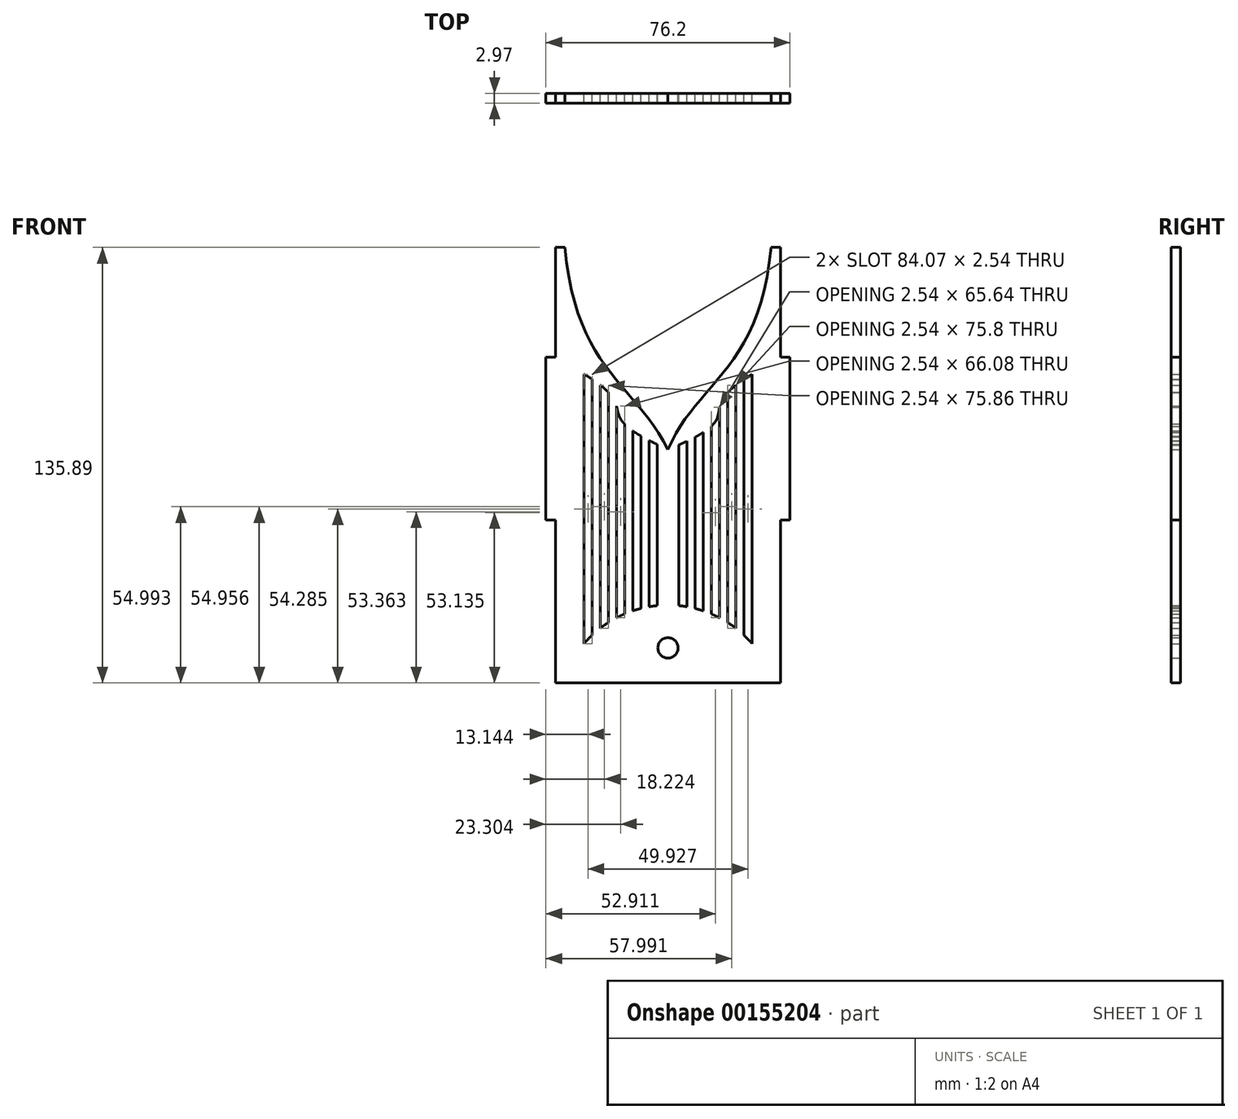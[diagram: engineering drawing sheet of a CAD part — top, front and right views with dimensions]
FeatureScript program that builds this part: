
annotation { "Feature Type Name" : "Feature", "Feature Type Description" : "" }
export const myFeature = defineFeature(function(context is Context, id is Id, definition is map)
    precondition{}
    {
        {
            var Q0;
            Q0=qCreatedBy(makeId("Front.planeOp"),FACE);
            var sketch = newSketch(context, id + "F0", { "sketchPlane" : qUnion([Q0])});
            skLineSegment(sketch, "E0", {"start": v(-13.59, -70.43) * mm, "end": v(56.67, -70.43) * mm});
            skLineSegment(sketch, "E1", {"start": v(-13.59, -70.43) * mm, "end": v(-13.59, 65.46) * mm});
            skLineSegment(sketch, "E2", {"start": v(56.67, -70.43) * mm, "end": v(56.67, 65.46) * mm});
            skLineSegment(sketch, "E3", {"start": v(-13.59, 65.46) * mm, "end": v(56.67, 65.46) * mm});
            skPoint(sketch, "E4.endSnap0", {"position": v(21.45, 21.63) * mm});
            skFitSpline(sketch, "E5", {"points": [v(-7.24, 27.36) * mm, v(-7.24, -61.54) * mm], "startDerivative": vector(0, -83.1) * mm, "endDerivative": vector(0, -83.1) * mm});
            skLineSegment(sketch, "E6", {"start": v(50.32, 27.36) * mm, "end": v(50.32, -61.54) * mm});
            skArc(sketch, "E7", {"start": v(50.32, -61.54) * mm, "mid": v(21.54, -46.15) * mm, "end": v(-7.24, -61.54) * mm});
            skFitSpline(sketch, "E8", {"points": [v(50.32, 27.36) * mm, v(21.54, 2.4) * mm], "startDerivative": vector(-74.85, -42.16) * mm, "endDerivative": vector(-86.33, -35.12) * mm});
            skFitSpline(sketch, "E9", {"points": [v(-7.24, 27.36) * mm, v(21.54, 2.4) * mm], "startDerivative": vector(73.06, -40.73) * mm, "endDerivative": vector(83.73, -37.5) * mm});
            skLineSegment(sketch, "E10", {"start": v(47.78, 25.88) * mm, "end": v(47.78, -58.2) * mm});
            skLineSegment(sketch, "E11", {"start": v(45.24, 24.26) * mm, "end": v(45.24, -55.54) * mm});
            skLineSegment(sketch, "E12", {"start": v(42.7, 22.42) * mm, "end": v(42.7, -53.37) * mm});
            skLineSegment(sketch, "E13", {"start": v(40.16, 20.13) * mm, "end": v(40.16, -51.59) * mm});
            skLineSegment(sketch, "E14", {"start": v(37.62, 15.52) * mm, "end": v(37.62, -50.11) * mm});
            skLineSegment(sketch, "E15", {"start": v(-4.69, 25.9) * mm, "end": v(-4.69, -58.18) * mm});
            skLineSegment(sketch, "E16", {"start": v(-2.15, 24.3) * mm, "end": v(-2.15, -55.53) * mm});
            skLineSegment(sketch, "E17", {"start": v(0.4, 22.5) * mm, "end": v(0.4, -53.37) * mm});
            skLineSegment(sketch, "E18", {"start": v(2.93, 20.25) * mm, "end": v(2.93, -51.58) * mm});
            skLineSegment(sketch, "E19", {"start": v(35.08, 9.62) * mm, "end": v(35.08, -48.9) * mm});
            skLineSegment(sketch, "E20", {"start": v(32.54, 7.7) * mm, "end": v(32.54, -47.95) * mm});
            skLineSegment(sketch, "E21", {"start": v(30, 6.24) * mm, "end": v(30, -47.2) * mm});
            skLineSegment(sketch, "E22", {"start": v(27.46, 4.97) * mm, "end": v(27.46, -46.66) * mm});
            skLineSegment(sketch, "E23", {"start": v(24.92, 3.82) * mm, "end": v(24.92, -46.32) * mm});
            skLineSegment(sketch, "E24", {"start": v(5.47, 15.97) * mm, "end": v(5.47, -50.1) * mm});
            skLineSegment(sketch, "E25", {"start": v(8.01, 10.3) * mm, "end": v(8.01, -48.9) * mm});
            skLineSegment(sketch, "E26", {"start": v(10.55, 8.22) * mm, "end": v(10.55, -47.94) * mm});
            skLineSegment(sketch, "E27", {"start": v(13.1, 6.61) * mm, "end": v(13.1, -47.2) * mm});
            skLineSegment(sketch, "E28", {"start": v(15.63, 5.22) * mm, "end": v(15.63, -46.66) * mm});
            skPoint(sketch, "E29.endSnap0", {"position": v(21.54, -46.15) * mm});
            skLineSegment(sketch, "E30", {"start": v(18.17, 3.96) * mm, "end": v(18.17, -46.32) * mm});
            skLineSegment(sketch, "E31", {"start": v(53.7, 65.46) * mm, "end": v(53.7, -70.43) * mm});
            skLineSegment(sketch, "E32.bottom", {"start": v(53.7, 31.17) * mm, "end": v(56.67, 31.17) * mm});
            skLineSegment(sketch, "E32.top", {"start": v(53.7, -19.63) * mm, "end": v(56.67, -19.63) * mm});
            skLineSegment(sketch, "E32.left", {"start": v(53.7, 31.17) * mm, "end": v(53.7, -19.63) * mm});
            skLineSegment(sketch, "E32.right", {"start": v(56.67, 31.17) * mm, "end": v(56.67, -19.63) * mm});
            skLineSegment(sketch, "E33", {"start": v(-10.61, 65.46) * mm, "end": v(-10.61, -70.43) * mm});
            skLineSegment(sketch, "E34.bottom", {"start": v(-13.59, 31.17) * mm, "end": v(-10.61, 31.17) * mm});
            skLineSegment(sketch, "E34.top", {"start": v(-13.59, -19.63) * mm, "end": v(-10.61, -19.63) * mm});
            skLineSegment(sketch, "E34.left", {"start": v(-13.59, 31.17) * mm, "end": v(-13.59, -19.63) * mm});
            skLineSegment(sketch, "E34.right", {"start": v(-10.61, 31.17) * mm, "end": v(-10.61, -19.63) * mm});
            skCircle(sketch, "E35", {"center": v(21.55, -59.5) * mm, "radius": 3.18 * mm});
            skLineSegment(sketch, "E36.bottom", {"start": v(-13.59, -19.63) * mm, "end": v(-16.56, -19.63) * mm});
            skLineSegment(sketch, "E36.top", {"start": v(-13.59, 31.17) * mm, "end": v(-16.56, 31.17) * mm});
            skLineSegment(sketch, "E36.left", {"start": v(-13.59, -19.63) * mm, "end": v(-13.59, 31.17) * mm});
            skLineSegment(sketch, "E36.right", {"start": v(-16.56, -19.63) * mm, "end": v(-16.56, 31.17) * mm});
            skLineSegment(sketch, "E37.bottom", {"start": v(56.67, 31.17) * mm, "end": v(59.64, 31.17) * mm});
            skLineSegment(sketch, "E37.top", {"start": v(56.67, -19.63) * mm, "end": v(59.64, -19.63) * mm});
            skLineSegment(sketch, "E37.right", {"start": v(59.64, 31.17) * mm, "end": v(59.64, -19.63) * mm});
            skFitSpline(sketch, "E38", {"points": [v(-10.61, 65.46) * mm, v(21.54, 2.4) * mm], "startDerivative": vector(10.13, -114.3) * mm, "endDerivative": vector(32.16, -63.07) * mm});
            skFitSpline(sketch, "E39", {"points": [v(53.7, 65.46) * mm, v(21.54, 2.4) * mm], "startDerivative": vector(-10.13, -114.3) * mm, "endDerivative": vector(-25.29, -61.13) * mm});
            skSolve(sketch);
        }
        {
            var Q0;
            Q0=makeQuery(id+"F0.imprint","IMPRINT",FACE,{"disambiguationData":[TD([[makeQuery(id+"F0.imprint","IMPRINT",EDGE,{"derivedFrom":sQuery(id+"F0.wireOp",EDGE,"E32.bottom")}),-1.0]])]});
            var Q1;
            Q1=makeQuery(id+"F0.imprint","IMPRINT",FACE,{"disambiguationData":[TD([[makeQuery(id+"F0.imprint","IMPRINT",EDGE,{"derivedFrom":sQuery(id+"F0.wireOp",EDGE,"E34.bottom")}),-1.0]])]});
            var Q2;
            Q2=makeQuery(id+"F0.imprint","IMPRINT",FACE,{"disambiguationData":[TD([[makeQuery(id+"F0.imprint","IMPRINT",EDGE,{"derivedFrom":sQuery(id+"F0.wireOp",EDGE,"6379b0e4-c35b-4f8c-ac63-970296725065")}),1.0]])]});
            var Q3;
            {var subQ0=sQuery(id+"F0.wireOp",EDGE,"E21");Q3=makeQuery(id+"F0.imprint","IMPRINT",FACE,{"disambiguationData":[TD([[makeQuery(id+"F0.imprint","IMPRINT",EDGE,{"derivedFrom":subQ0}),-1.0]])]});}
            var Q4;
            {var subQ0=sQuery(id+"F0.wireOp",EDGE,"E19");Q4=makeQuery(id+"F0.imprint","IMPRINT",FACE,{"disambiguationData":[TD([[makeQuery(id+"F0.imprint","IMPRINT",EDGE,{"derivedFrom":subQ0}),-1.0]])]});}
            var Q5;
            {var subQ0=sQuery(id+"F0.wireOp",EDGE,"E13");Q5=makeQuery(id+"F0.imprint","IMPRINT",FACE,{"disambiguationData":[TD([[makeQuery(id+"F0.imprint","IMPRINT",EDGE,{"derivedFrom":subQ0}),-1.0]])]});}
            var Q6;
            {var subQ0=sQuery(id+"F0.wireOp",EDGE,"E11");Q6=makeQuery(id+"F0.imprint","IMPRINT",FACE,{"disambiguationData":[TD([[makeQuery(id+"F0.imprint","IMPRINT",EDGE,{"derivedFrom":subQ0}),-1.0]])]});}
            var Q7;
            {var subQ0=sQuery(id+"F0.wireOp",EDGE,"E6");Q7=makeQuery(id+"F0.imprint","IMPRINT",FACE,{"disambiguationData":[TD([[makeQuery(id+"F0.imprint","IMPRINT",EDGE,{"derivedFrom":subQ0}),-1.0]])]});}
            var Q8;
            {var subQ0=sQuery(id+"F0.wireOp",EDGE,"E23");Q8=makeQuery(id+"F0.imprint","IMPRINT",FACE,{"disambiguationData":[TD([[makeQuery(id+"F0.imprint","IMPRINT",EDGE,{"derivedFrom":subQ0}),-1.0]])]});}
            var Q9;
            {var subQ0=sQuery(id+"F0.wireOp",EDGE,"E27");Q9=makeQuery(id+"F0.imprint","IMPRINT",FACE,{"disambiguationData":[TD([[makeQuery(id+"F0.imprint","IMPRINT",EDGE,{"derivedFrom":subQ0}),1.0]])]});}
            var Q10;
            {var subQ0=sQuery(id+"F0.wireOp",EDGE,"E25");Q10=makeQuery(id+"F0.imprint","IMPRINT",FACE,{"disambiguationData":[TD([[makeQuery(id+"F0.imprint","IMPRINT",EDGE,{"derivedFrom":subQ0}),1.0]])]});}
            var Q11;
            {var subQ0=sQuery(id+"F0.wireOp",EDGE,"E18");Q11=makeQuery(id+"F0.imprint","IMPRINT",FACE,{"disambiguationData":[TD([[makeQuery(id+"F0.imprint","IMPRINT",EDGE,{"derivedFrom":subQ0}),1.0]])]});}
            var Q12;
            {var subQ0=sQuery(id+"F0.wireOp",EDGE,"E16");Q12=makeQuery(id+"F0.imprint","IMPRINT",FACE,{"disambiguationData":[TD([[makeQuery(id+"F0.imprint","IMPRINT",EDGE,{"derivedFrom":subQ0}),1.0]])]});}
            var Q13;
            {var subQ0=sQuery(id+"F0.wireOp",EDGE,"E5");Q13=makeQuery(id+"F0.imprint","IMPRINT",FACE,{"disambiguationData":[TD([[makeQuery(id+"F0.imprint","IMPRINT",EDGE,{"derivedFrom":subQ0}),1.0]])]});}
            var Q14;
            {var subQ3=sQuery(id+"F0.wireOp",EDGE,"E34.bottom");Q14=makeQuery(id+"F0.imprint","IMPRINT",FACE,{"disambiguationData":[TD([[makeQuery(id+"F0.imprint","IMPRINT",EDGE,{"derivedFrom":subQ3}),1.0]])]});}
            var Q15;
            Q15=makeQuery(id+"F0.imprint","IMPRINT",FACE,{"disambiguationData":[TD([[makeQuery(id+"F0.imprint","IMPRINT",EDGE,{"derivedFrom":sQuery(id+"F0.wireOp",EDGE,"E36.bottom")}),-1.0]])]});
            var Q16;
            {var subQ5=sQuery(id+"F0.wireOp",EDGE,"E34.top");Q16=makeQuery(id+"F0.imprint","IMPRINT",FACE,{"disambiguationData":[TD([[makeQuery(id+"F0.imprint","IMPRINT",EDGE,{"derivedFrom":subQ5}),-1.0]])]});}
            var Q17;
            {var subQ3=sQuery(id+"F0.wireOp",EDGE,"E32.bottom");Q17=makeQuery(id+"F0.imprint","IMPRINT",FACE,{"disambiguationData":[TD([[makeQuery(id+"F0.imprint","IMPRINT",EDGE,{"derivedFrom":subQ3}),1.0]])]});}
            var Q18;
            {var subQ5=sQuery(id+"F0.wireOp",EDGE,"E32.top");Q18=makeQuery(id+"F0.imprint","IMPRINT",FACE,{"disambiguationData":[TD([[makeQuery(id+"F0.imprint","IMPRINT",EDGE,{"derivedFrom":subQ5}),-1.0]])]});}
            var Q19;
            Q19=makeQuery(id+"F0.imprint","IMPRINT",FACE,{"disambiguationData":[TD([[makeQuery(id+"F0.imprint","IMPRINT",EDGE,{"derivedFrom":sQuery(id+"F0.wireOp",EDGE,"E37.bottom")}),-1.0]])]});
            var Q20;
            {var subQ20=sQuery(id+"F0.wireOp",EDGE,"E5");Q20=makeQuery(id+"F0.imprint","IMPRINT",FACE,{"disambiguationData":[TD([[makeQuery(id+"F0.imprint","IMPRINT",EDGE,{"derivedFrom":subQ20}),-1.0]])]});}
            extrude(context, id + "F1", {"entities" : qUnion([Q0, Q1, Q2, Q3, Q4, Q5, Q6, Q7, Q8, Q9, Q10, Q11, Q12, Q13, Q14, Q15, Q16, Q17, Q18, Q19, Q20]), "depth" : 2.97 * mm});
        }
    });
